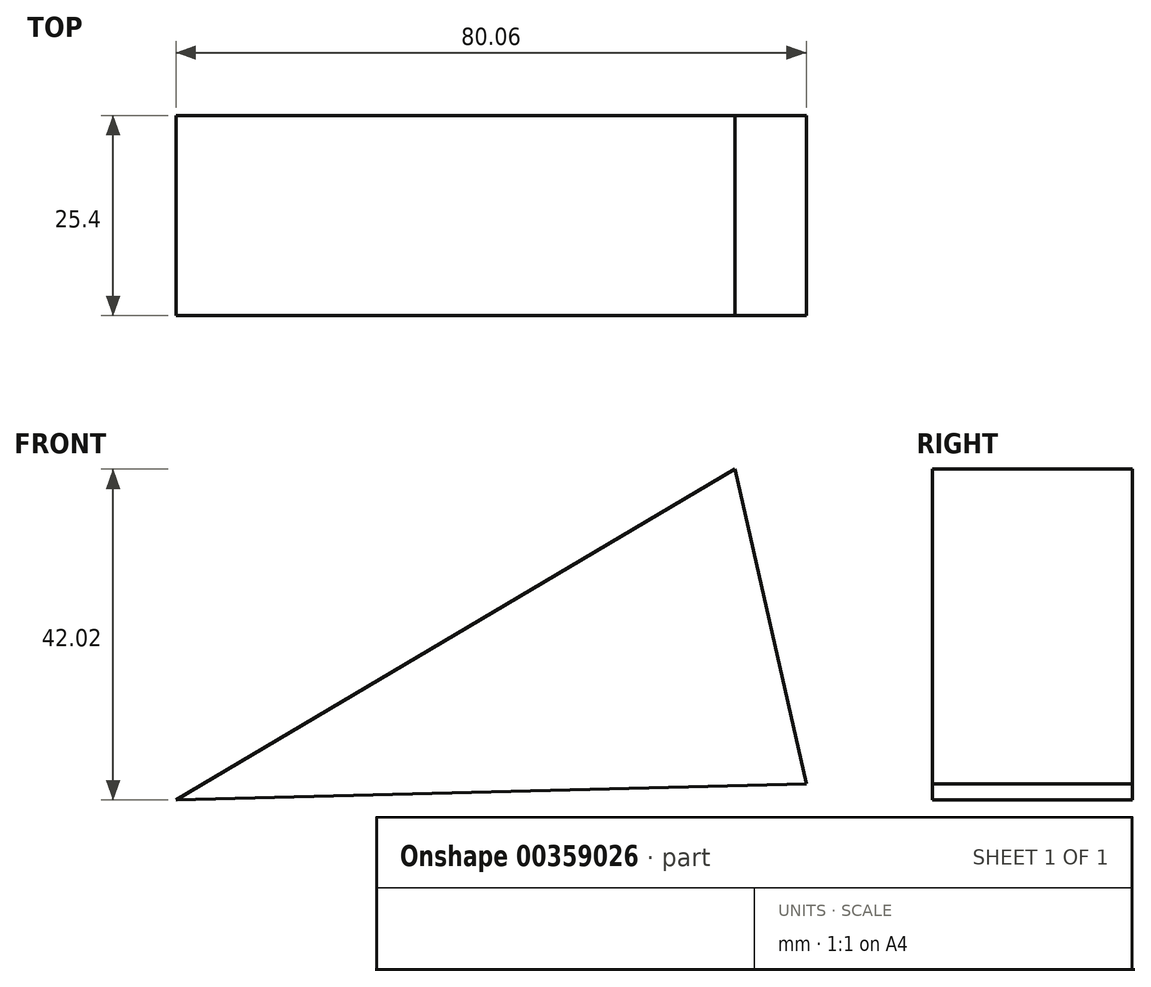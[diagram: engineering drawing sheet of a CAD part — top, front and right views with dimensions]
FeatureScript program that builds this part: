
annotation { "Feature Type Name" : "Feature", "Feature Type Description" : "" }
export const myFeature = defineFeature(function(context is Context, id is Id, definition is map)
    precondition{}
    {
        {
            var Q0;
            Q0=qCreatedBy(makeId("Front.planeOp"),FACE);
            var sketch = newSketch(context, id + "F0", { "sketchPlane" : qUnion([Q0])});
            skLineSegment(sketch, "E0", {"start": v(-105.24, -19.83) * mm, "end": v(-34.22, 22.19) * mm});
            skLineSegment(sketch, "E1", {"start": v(-34.22, 22.19) * mm, "end": v(-25.18, -17.81) * mm});
            skLineSegment(sketch, "E2", {"start": v(-105.24, -19.83) * mm, "end": v(-25.18, -17.81) * mm});
            skSolve(sketch);
        }
        {
            var Q0;
            Q0=makeQuery(id+"F0.imprint","IMPRINT",FACE,{"disambiguationData":[TD([[makeQuery(id+"F0.imprint","IMPRINT",EDGE,{"derivedFrom":sQuery(id+"F0.wireOp",EDGE,"E0")}),-1.0]])]});
            extrude(context, id + "F1", {"entities" : qUnion([Q0]), "depth" : 25.4 * mm});
        }
    });
